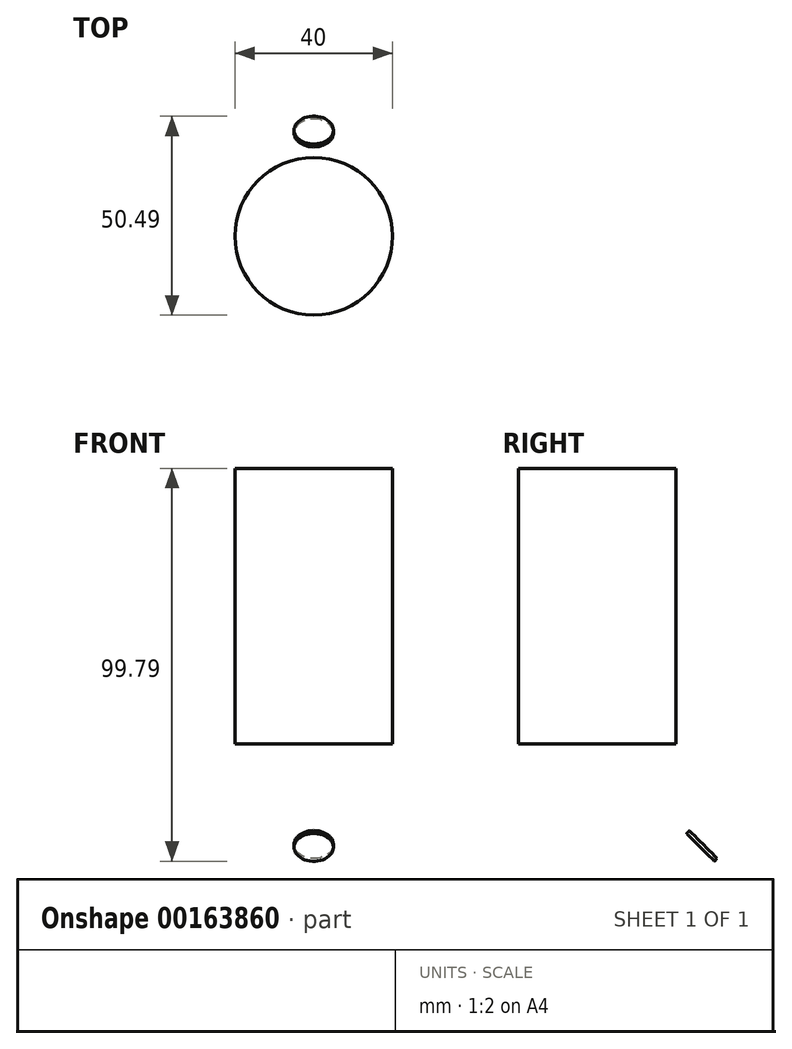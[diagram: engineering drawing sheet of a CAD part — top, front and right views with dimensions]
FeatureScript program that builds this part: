
annotation { "Feature Type Name" : "Feature", "Feature Type Description" : "" }
export const myFeature = defineFeature(function(context is Context, id is Id, definition is map)
    precondition{}
    {
        {
            var Q0;
            Q0=qCreatedBy(makeId("Top.planeOp"),FACE);
            var sketch = newSketch(context, id + "F0", { "sketchPlane" : qUnion([Q0])});
            skCircle(sketch, "E0", {"center": v(0, 0) * mm, "radius": 20 * mm});
            skSolve(sketch);
        }
        {
            var Q0;
            Q0=makeQuery(id+"F0.imprint","IMPRINT",FACE,{"disambiguationData":[TD([[makeQuery(id+"F0.imprint","IMPRINT",EDGE,{"derivedFrom":sQuery(id+"F0.wireOp",EDGE,"E0")}),1.0]])]});
            extrude(context, id + "F1", {"entities" : qUnion([Q0]), "depth" : 70 * mm});
        }
        {
            var Q0;
            Q0=qCreatedBy(makeId("Top.planeOp"),FACE);
            var sketch = newSketch(context, id + "F2", { "sketchPlane" : qUnion([Q0])});
            skLineSegment(sketch, "E1", {"start": v(-75.38, 0) * mm, "end": v(75.08, 0) * mm});
            skSolve(sketch);
        }
        {
            var Q0;
            Q0=sQuery(id+"F2.wireOp",EDGE,"E1");
            cPlane(context, id + "F3", {"entities" : qUnion([Q0]), "cplaneType" : CPlaneType.LINE_ANGLE, "offset" : 25 * mm, "angle" : 45 * degree, "width" : 150 * mm, "height" : 150 * mm});
        }
        {
            var Q0;
            Q0=qCreatedBy(id+"F3.planeOp",FACE);
            var sketch = newSketch(context, id + "F4", { "sketchPlane" : qUnion([Q0])});
            skCircle(sketch, "E2", {"center": v(0, -37.12) * mm, "radius": 5 * mm});
            skLineSegment(sketch, "E3", {"start": v(0, -42.12) * mm, "end": v(0, -32.12) * mm});
            skSolve(sketch);
        }
        {
            var Q0;
            {var subQ0=sQuery(id+"F4.wireOp",EDGE,"E3");Q0=makeQuery(id+"F4.imprint","IMPRINT",FACE,{"disambiguationData":[TD([[makeQuery(id+"F4.imprint","IMPRINT",EDGE,{"derivedFrom":subQ0}),-1.0]])]});}
            var Q1;
            {var subQ0=sQuery(id+"F4.wireOp",EDGE,"E3");Q1=makeQuery(id+"F4.imprint","IMPRINT",FACE,{"disambiguationData":[TD([[makeQuery(id+"F4.imprint","IMPRINT",EDGE,{"derivedFrom":subQ0}),1.0]])]});}
            extrude(context, id + "F5", {"entities" : qUnion([Q0, Q1]), "depth" : 1 * mm});
        }
    });
